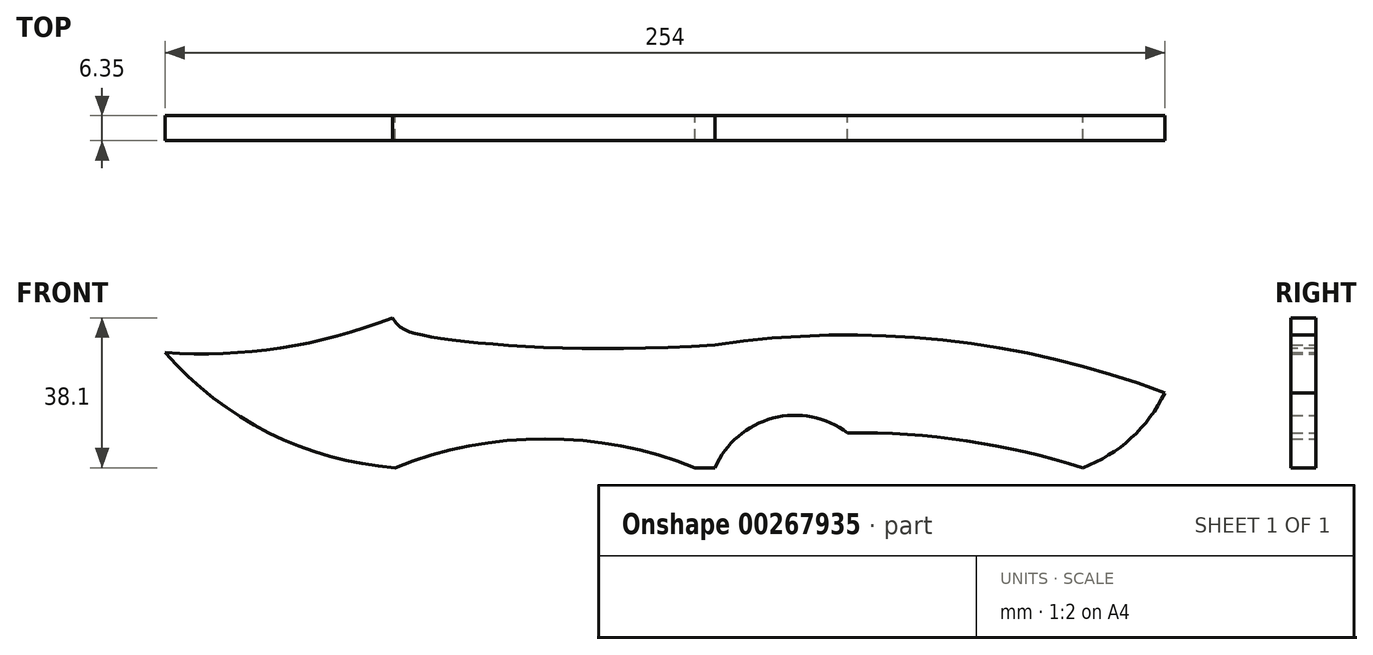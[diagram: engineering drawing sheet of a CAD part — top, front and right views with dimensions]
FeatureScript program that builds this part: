
annotation { "Feature Type Name" : "Feature", "Feature Type Description" : "" }
export const myFeature = defineFeature(function(context is Context, id is Id, definition is map)
    precondition{}
    {
        {
            var Q0;
            Q0=qCreatedBy(makeId("Front.planeOp"),FACE);
            var sketch = newSketch(context, id + "F0", { "sketchPlane" : qUnion([Q0])});
            skLineSegment(sketch, "E0.bottom", {"start": v(-127, 19.05) * mm, "end": v(127, 19.05) * mm});
            skLineSegment(sketch, "E0.top", {"start": v(-127, -19.05) * mm, "end": v(127, -19.05) * mm});
            skLineSegment(sketch, "E0.left", {"start": v(-127, 19.05) * mm, "end": v(-127, -19.05) * mm});
            skLineSegment(sketch, "E0.right", {"start": v(127, 19.05) * mm, "end": v(127, -19.05) * mm});
            skPoint(sketch, "E0.middle", {"position": v(0, 0) * mm});
            skLineSegment(sketch, "E1", {"start": v(12.7, 19.05) * mm, "end": v(12.7, -19.05) * mm, "construction": true});
            skCircle(sketch, "E2", {"center": v(33.07, -27.94) * mm, "radius": 22.23 * mm});
            skArc(sketch, "E3", {"start": v(106.17, -19.05) * mm, "mid": v(118.42, -11.52) * mm, "end": v(127, 0) * mm});
            skArc(sketch, "E4", {"start": v(106.17, -19.05) * mm, "mid": v(76.64, -12.22) * mm, "end": v(46.4, -10.16) * mm});
            skArc(sketch, "E5", {"start": v(7.62, -19.05) * mm, "mid": v(-30.48, -11.71) * mm, "end": v(-68.58, -19.05) * mm});
            skArc(sketch, "E6", {"start": v(127, 0) * mm, "mid": v(70.63, 13.39) * mm, "end": v(12.7, 12.18) * mm});
            skFitSpline(sketch, "E7", {"points": [v(-69.27, 19.05) * mm, v(-62.1, 14.74) * mm, v(12.7, 12.18) * mm], "startDerivative": vector(23.4, -33.82) * mm, "endDerivative": vector(139.58, 9.7) * mm});
            skArc(sketch, "E8", {"start": v(-127, 10.25) * mm, "mid": v(-97.64, 11.4) * mm, "end": v(-69.27, 19.05) * mm});
            skArc(sketch, "E9", {"start": v(-127, 10.25) * mm, "mid": v(-100.67, -10.15) * mm, "end": v(-68.58, -19.05) * mm});
            skSolve(sketch);
        }
        {
            var Q0;
            Q0=makeQuery(id+"F0.imprint","IMPRINT",FACE,{"disambiguationData":[TD([[makeQuery(id+"F0.imprint","IMPRINT",EDGE,{"derivedFrom":sQuery(id+"F0.wireOp",EDGE,"E3")}),1.0]])]});
            extrude(context, id + "F1", {"entities" : qUnion([Q0]), "depth" : 6.35 * mm, "offsetDistance" : 25.4 * mm});
        }
    });
